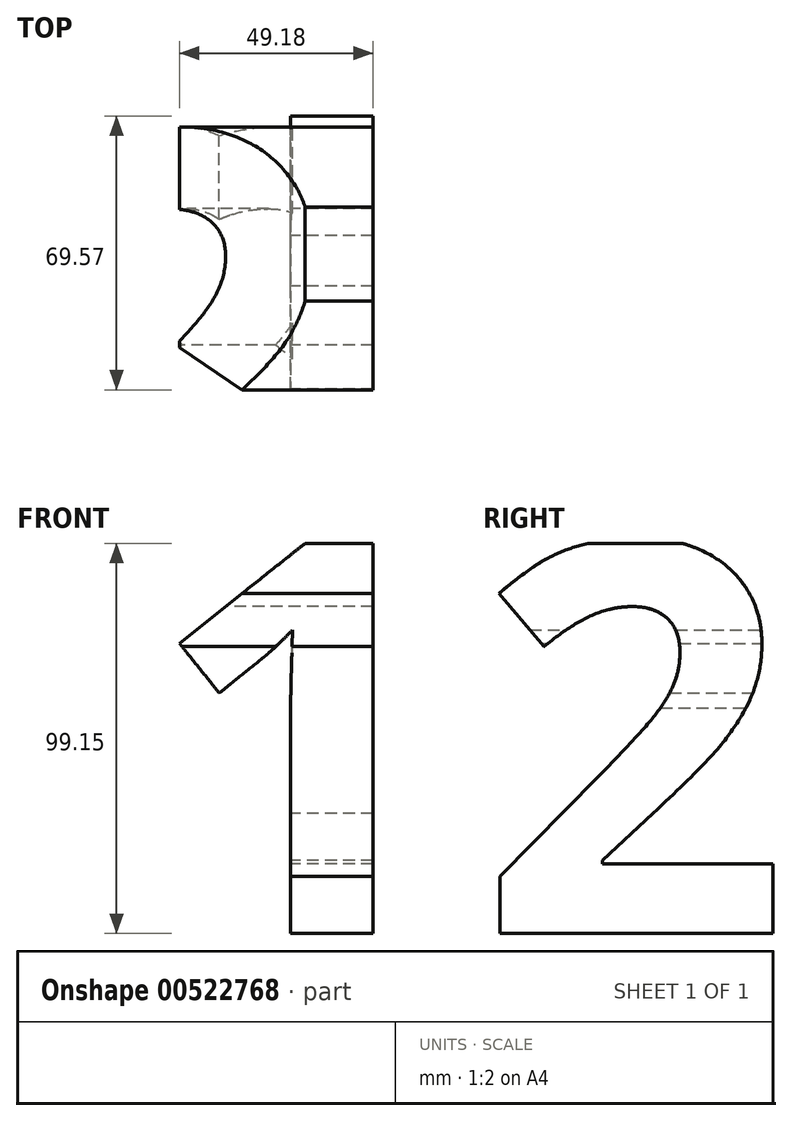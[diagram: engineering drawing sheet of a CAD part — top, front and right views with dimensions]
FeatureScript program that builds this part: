
annotation { "Feature Type Name" : "Feature", "Feature Type Description" : "" }
export const myFeature = defineFeature(function(context is Context, id is Id, definition is map)
    precondition{}
    {
        {
            var Q0;
            Q0=qCreatedBy(makeId("Front.planeOp"),FACE);
            var sketch = newSketch(context, id + "F0", { "sketchPlane" : qUnion([Q0])});
            skText(sketch, "E0", { "text": "1", "fontName": "OpenSans-Bold.ttf"});
            const initialGuessF0  = {"E0": [-0.0332, -0.05, 1, 0, 0.1]};
            skSetInitialGuess(sketch, initialGuessF0);
            skSolve(sketch);
        }
        {
            var Q0;
            Q0=qCreatedBy(makeId("Right.planeOp"),FACE);
            var sketch = newSketch(context, id + "F1", { "sketchPlane" : qUnion([Q0])});
            skText(sketch, "E1", { "text": "2", "fontName": "OpenSans-Bold.ttf"});
            const initialGuessF1  = {"E1": [-0.04194, -0.05, 1, 0, 0.1]};
            skSetInitialGuess(sketch, initialGuessF1);
            skSolve(sketch);
        }
        {
            var Q0;
            Q0=makeQuery(id+"F1.imprint","IMPRINT",FACE,{"disambiguationData":[TD([[makeQuery(id+"F1.imprint","IMPRINT",EDGE,{"derivedFrom":sQuery(id+"F1.wireOp",EDGE,"E1.sketch_text.stroke-0")}),-1.0]])]});
            extrude(context, id + "F2", {"entities" : qUnion([Q0]), "depth" : 50 * mm, "offsetDistance" : 25 * mm, "hasSecondDirection" : true, "secondDirectionOppositeDirection" : true, "secondDirectionDepth" : 50 * mm});
        }
        {
            var Q0;
            Q0=makeQuery(id+"F0.imprint","IMPRINT",FACE,{"disambiguationData":[TD([[makeQuery(id+"F0.imprint","IMPRINT",EDGE,{"derivedFrom":sQuery(id+"F0.wireOp",EDGE,"E0.sketch_text.stroke-0")}),-1.0]])]});
            extrude(context, id + "F3", {"entities" : qUnion([Q0]), "operationType" : NewBodyOperationType.INTERSECT, "depth" : 50 * mm, "offsetDistance" : 25 * mm, "hasSecondDirection" : true, "secondDirectionOppositeDirection" : true, "secondDirectionDepth" : 50 * mm});
        }
    });
